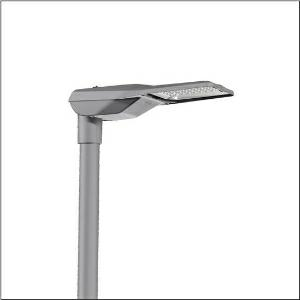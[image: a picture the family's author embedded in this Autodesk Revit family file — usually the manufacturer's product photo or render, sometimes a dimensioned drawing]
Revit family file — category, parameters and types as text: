
# Revit family: streetlight_sl_21_mini___p0_5a_5xe2v33s08gb_4fda
name_source: partatom
category: Lighting Fixtures
units: mm (PartAtom-declared; Revit-internal decimal feet)

## family parameters
Cut with Voids When Loaded = No
Host = Face
Light Source = No
Part Type = Normal
Room Calculation Point = No
Round Connector Dimension = Use Diameter
Shared = No

## types (1)
- --- (1 x LED, 5840 lm, 40.4 W, 3000K)
    Apparent Load = 40 VA
    CIE Flux Codes = 37 73 96 100 100
    Color Rendering = 70
    Color Temperature = 3000K
    Default Elevation = 1800 mm
    Description = Streetlight SL 21 mini, mast luminaire, primary light control with lens, of PMMA, primary optical cover: cover, of toughened safety glass, transparent, light distribution: P0.5a, light emission: direct distribution, primary light characteristic: asymmetric, installation type: post-top, side-entry, LED, High Power LED, rated luminous flux: 5.840lm, luminous efficacy: 145lm/W, light colour: 730, colour temperature: 3000K, control gear: D4i, control: pre-setting: logarithmic dimming characteristic, flexible luminous flux parameterisation, time-dependent luminous flux control, constant luminous flux control, overheat protection, mains connection: 220..240V, AC, 50/60Hz, start of lifetime: 40W, end of service life: 41W, reduction: 19W, luminaire housing, of diecast aluminium, powder-coated, Siteco® metallic grey (DB 702S), corrosivity category C5 mid according to DIN EN ISO 12944, multi-level sealing system, sealing non-destructively replaceable, inclination adjustable: 0°, 5°, 10°, 15°, please order mast flange separately, length: 628mm, width: 235mm, height: 110mm, mast flange for spigot size: 42mm (side-entry): 5XC10008XM4, 60/48mm (side-entry/post-top): 5XC10108XM2, 76/60mm (side-entry/post-top): 5XC10108XM1, mounting height: 4..8m, Smart Interface above, protection rating (complete): IP66, insulation class (complete): insulation class II (safety insulation), certification: CE, ENEC, ENEC+, VDE, impact resistance: IK09, permissible operating ambient temperature for outdoor applications: -40..+50°C, standard-compliant lighting for roads and squares, packaging unit: 1 piece

Light Distribution: P0.5a
    Height = 110 mm
    Lamp = 1 x LED
    Lamp Light Flux = 5840 lm
    Lamp Power = 40.4 W
    Lamp count = 1
    Length = 625 mm
    Luminous efficacy = 145 lm/W
    Manufacturer = Siteco
    ModVariant = No
    Model = 5XE2V33S08GB
    Number of Poles = 1
    OnlyDefault = Yes
    Power Factor = 1
    Product Name = Streetlight SL 21 mini | P0.5a
    Product group = mast luminaire | pylon top
    ProductGroupID = 6100
    Protection Class = Protection class II
    Protection Degree = IP 66
    RLX_Detail_Level = 1
    RLX_Emergency_Light_Flux = 0 lm
    RLX_Emergency_Type = 0
    RLX_Emergency_Type_DB = No
    RlxData = <blob elided: 93461 chars, md5=5570f84a>
    Socket = socket
    Standby Power = 0 W
    System Light Flux = 5840 lm
    System Power = 40 W
    Type Comments = factory setting: luminous flux: 100 % | dim-lin: 254 | 812 mA
    Type Image = l_1003515.jpg
    URL = http://relux.com
    VarID = @adj_066470
    Voltage = 0 V
    Weight = 0.00 kg
    Width = 234 mm

## geometry (parser evidence)
native form markers: Blend x4, Sweep x11
no freeform markers — native parametric forms only
